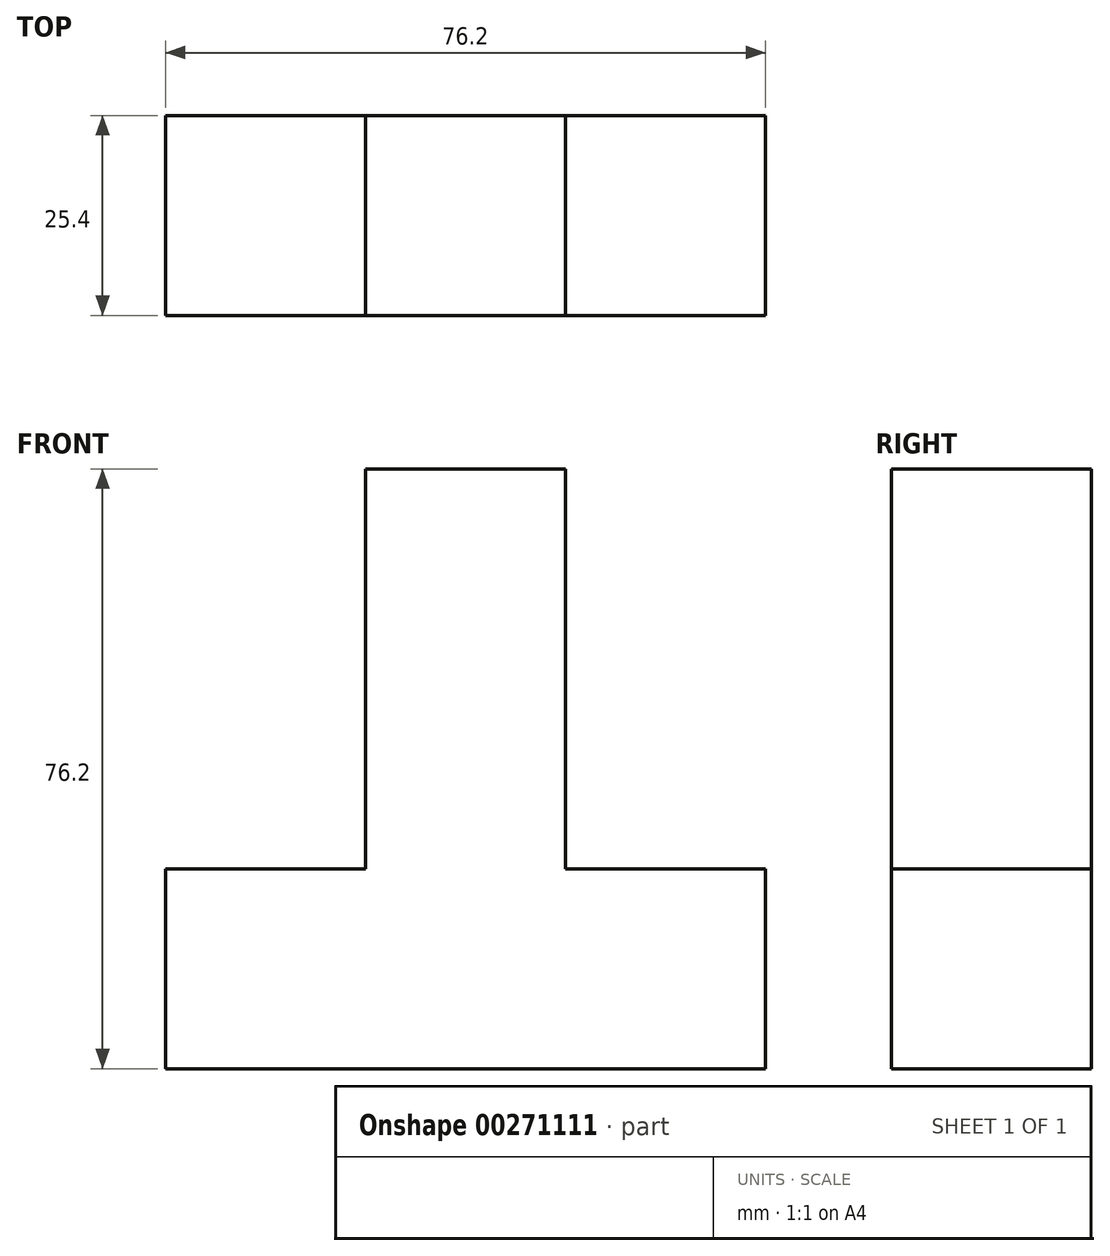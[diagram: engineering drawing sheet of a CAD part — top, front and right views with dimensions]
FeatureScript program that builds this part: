
annotation { "Feature Type Name" : "Feature", "Feature Type Description" : "" }
export const myFeature = defineFeature(function(context is Context, id is Id, definition is map)
    precondition{}
    {
        {
            var Q0;
            Q0=qCreatedBy(makeId("Front.planeOp"),FACE);
            var sketch = newSketch(context, id + "F0", { "sketchPlane" : qUnion([Q0])});
            skLineSegment(sketch, "E0", {"start": v(0, 0) * mm, "end": v(-76.2, 0) * mm});
            skLineSegment(sketch, "E1", {"start": v(-76.2, 0) * mm, "end": v(-76.2, 25.4) * mm});
            skLineSegment(sketch, "E2", {"start": v(0, 0) * mm, "end": v(0, 25.4) * mm});
            skLineSegment(sketch, "E3", {"start": v(0, 25.4) * mm, "end": v(-25.4, 25.4) * mm});
            skLineSegment(sketch, "E4", {"start": v(-76.2, 25.4) * mm, "end": v(-50.8, 25.4) * mm});
            skLineSegment(sketch, "E5", {"start": v(-50.8, 25.4) * mm, "end": v(-50.8, 76.2) * mm});
            skLineSegment(sketch, "E6", {"start": v(-50.8, 76.2) * mm, "end": v(-25.4, 76.2) * mm});
            skLineSegment(sketch, "E7", {"start": v(-25.4, 76.2) * mm, "end": v(-25.4, 25.4) * mm});
            skSolve(sketch);
        }
        {
            var Q0;
            Q0=makeQuery(id+"F0.imprint","IMPRINT",FACE,{"disambiguationData":[TD([[makeQuery(id+"F0.imprint","IMPRINT",EDGE,{"derivedFrom":sQuery(id+"F0.wireOp",EDGE,"E0")}),-1.0]])]});
            extrude(context, id + "F1", {"entities" : qUnion([Q0]), "depth" : 25.4 * mm});
        }
    });
